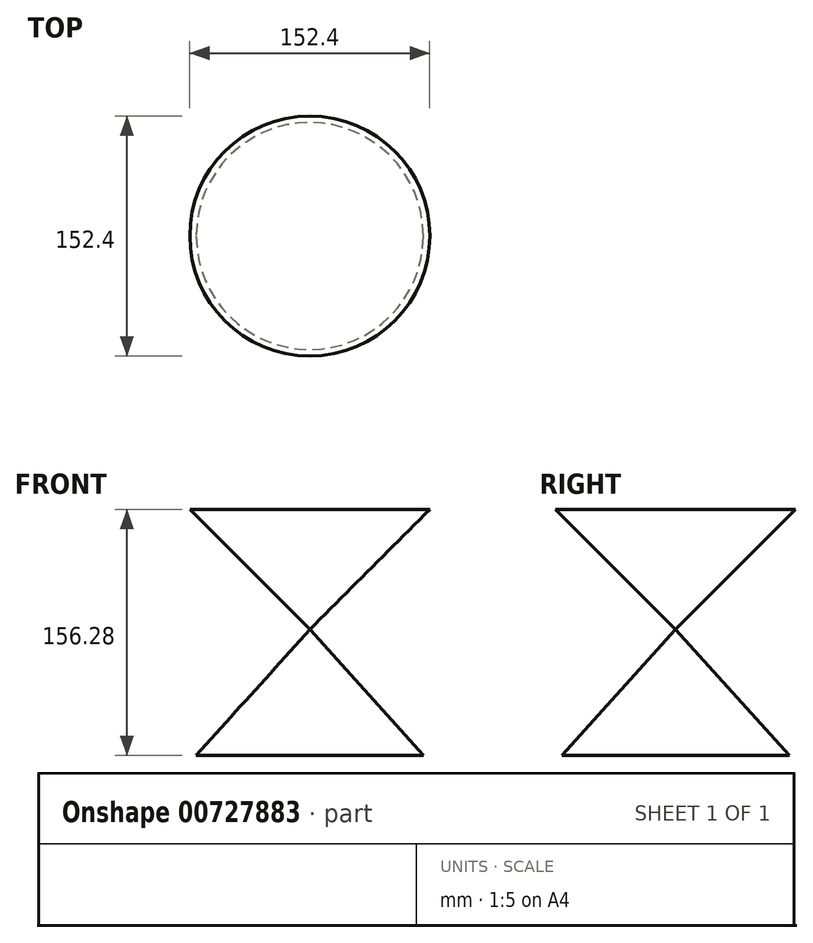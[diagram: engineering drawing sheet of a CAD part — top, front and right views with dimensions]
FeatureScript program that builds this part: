
annotation { "Feature Type Name" : "Feature", "Feature Type Description" : "" }
export const myFeature = defineFeature(function(context is Context, id is Id, definition is map)
    precondition{}
    {
        {
            var Q0;
            Q0=qCreatedBy(makeId("Front.planeOp"),FACE);
            var sketch = newSketch(context, id + "F0", { "sketchPlane" : qUnion([Q0])});
            skLineSegment(sketch, "E0", {"start": v(23.28, 75.44) * mm, "end": v(-52.92, 75.44) * mm});
            skLineSegment(sketch, "E1", {"start": v(19.2, -80.84) * mm, "end": v(-52.92, -0.76) * mm});
            skLineSegment(sketch, "E2.MirrorCS", {"start": v(19.2, -80.84) * mm, "end": v(-52.92, -80.84) * mm});
            skLineSegment(sketch, "E3", {"start": v(-52.92, -0.76) * mm, "end": v(23.28, 75.44) * mm});
            skLineSegment(sketch, "E4", {"start": v(-52.92, 75.44) * mm, "end": v(-52.92, -80.84) * mm});
            skSolve(sketch);
        }
        {
            var Q0;
            {var subQ0=sQuery(id+"F0.wireOp",EDGE,"E0");Q0=makeQuery(id+"F0.imprint","IMPRINT",FACE,{"disambiguationData":[TD([[makeQuery(id+"F0.imprint","IMPRINT",EDGE,{"derivedFrom":subQ0}),1.0]])]});}
            var Q1;
            {var subQ0=sQuery(id+"F0.wireOp",EDGE,"E1");Q1=makeQuery(id+"F0.imprint","IMPRINT",FACE,{"disambiguationData":[TD([[makeQuery(id+"F0.imprint","IMPRINT",EDGE,{"derivedFrom":subQ0}),1.0]])]});}
            var Q2;
            Q2=sQuery(id+"F0.wireOp",EDGE,"E2.MirrorCS");
            var Q3;
            Q3=sQuery(id+"F0.wireOp",EDGE,"E1");
            var Q4;
            Q4=sQuery(id+"F0.wireOp",EDGE,"E4");
            revolve(context, id + "F1", {"surfaceOperationType" : NewSurfaceOperationType.NEW, "entities" : qUnion([Q0, Q1]), "surfaceEntities" : qUnion([Q2, Q3]), "axis" : qUnion([Q4]), "revolveType" : RevolveType.FULL});
        }
        {
            var Q0;
            Q0=sQuery(id+"F0.wireOp",EDGE,"E3");
            var Q1;
            Q1=sQuery(id+"F0.wireOp",EDGE,"E0");
            var Q2;
            Q2=sQuery(id+"F0.wireOp",EDGE,"E4");
            revolve(context, id + "F2", {"bodyType" : ToolBodyType.SURFACE, "surfaceOperationType" : NewSurfaceOperationType.NEW, "surfaceEntities" : qUnion([Q0, Q1]), "axis" : qUnion([Q2]), "revolveType" : RevolveType.FULL});
        }
    });
